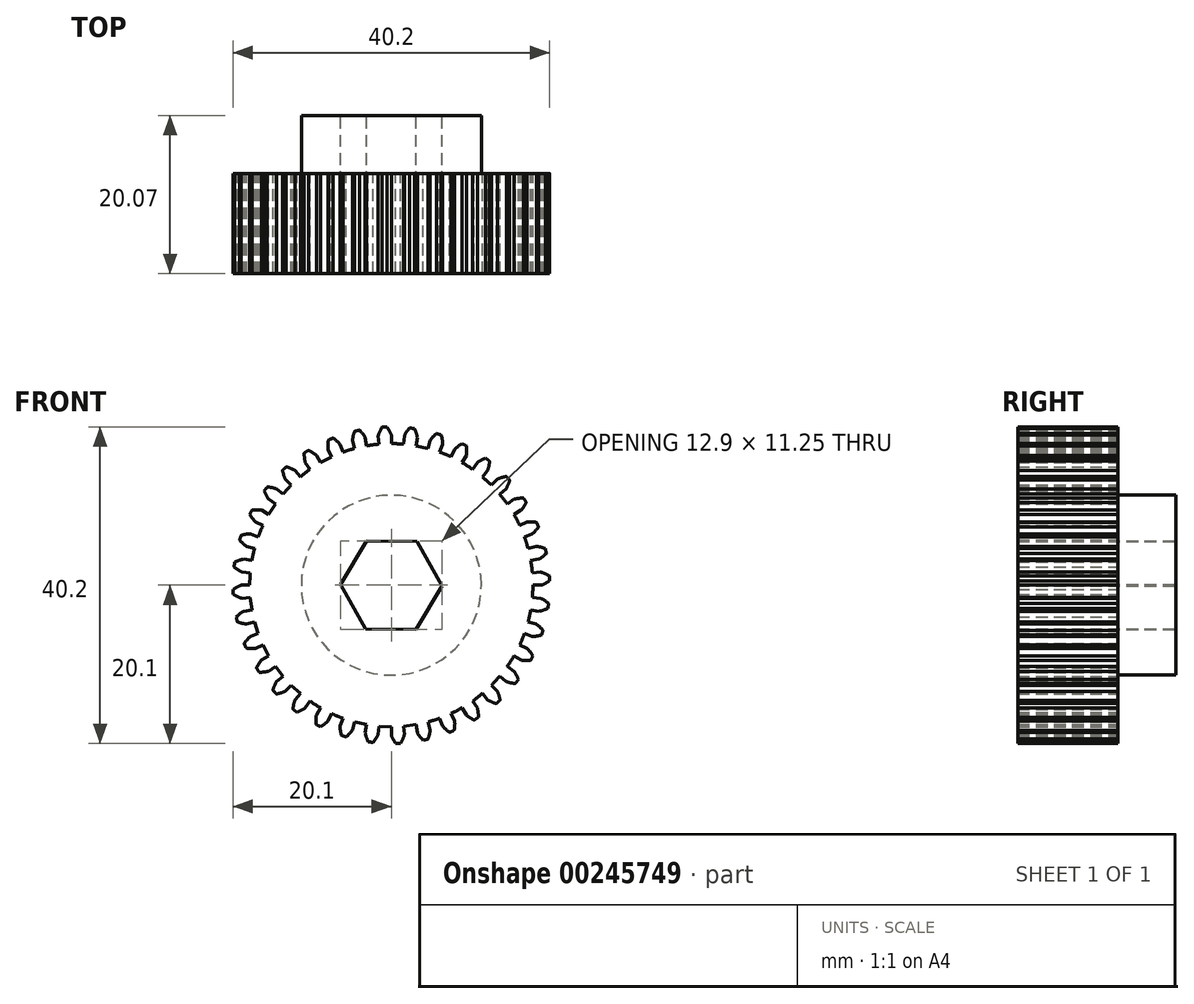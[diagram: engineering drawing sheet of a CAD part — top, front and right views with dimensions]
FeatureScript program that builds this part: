
annotation { "Feature Type Name" : "Feature", "Feature Type Description" : "" }
export const myFeature = defineFeature(function(context is Context, id is Id, definition is map)
    precondition{}
    {
        {
            var Q0;
            Q0=qCreatedBy(makeId("Front.planeOp"),FACE);
            var sketch = newSketch(context, id + "F0", { "sketchPlane" : qUnion([Q0])});
            skArc(sketch, "E0", {"start": v(-1.57, 17.91) * mm, "mid": v(-2.35, 17.83) * mm, "end": v(-3.12, 17.7) * mm});
            skLineSegment(sketch, "E1", {"start": v(0, 0) * mm, "end": v(0, 34.59) * mm});
            skLineSegment(sketch, "E2", {"start": v(0, 0) * mm, "end": v(-1.61, 36.93) * mm, "construction": true});
            skArc(sketch, "E3.trimOffspring", {"start": v(0, 19.05) * mm, "mid": v(-0.25, 19.6) * mm, "end": v(-0.56, 20.1) * mm});
            skArc(sketch, "E4.trimOffspring", {"start": v(-4.48, 17.42) * mm, "mid": v(-4.47, 17.42) * mm, "end": v(-4.47, 17.42) * mm});
            skArc(sketch, "E5.trimOffspring", {"start": v(-0.56, 20.1) * mm, "mid": v(-0.72, 20.1) * mm, "end": v(-0.88, 20.08) * mm});
            skLineSegment(sketch, "E6", {"start": v(0, 19.05) * mm, "end": v(0, 17.98) * mm});
            skArc(sketch, "E7.MirrorCS", {"start": v(-1.2, 20.07) * mm, "mid": v(-1.03, 20.08) * mm, "end": v(-0.88, 20.08) * mm});
            skArc(sketch, "E8.MirrorCS", {"start": v(-1.66, 18.98) * mm, "mid": v(-1.46, 19.54) * mm, "end": v(-1.2, 20.07) * mm});
            skLineSegment(sketch, "E9.MirrorCS", {"start": v(-1.66, 18.98) * mm, "end": v(-1.57, 17.91) * mm});
            skArc(sketch, "E10.1.0", {"start": v(-3.3, 18.76) * mm, "mid": v(-3.65, 19.25) * mm, "end": v(-4.04, 19.7) * mm});
            skArc(sketch, "E10.1.1", {"start": v(-4.93, 18.4) * mm, "mid": v(-4.83, 18.99) * mm, "end": v(-4.66, 19.56) * mm});
            skArc(sketch, "E10.1.2", {"start": v(-4.04, 19.7) * mm, "mid": v(-4.2, 19.66) * mm, "end": v(-4.35, 19.63) * mm});
            skArc(sketch, "E10.1.3", {"start": v(-4.66, 19.56) * mm, "mid": v(-4.5, 19.6) * mm, "end": v(-4.35, 19.63) * mm});
            skLineSegment(sketch, "E10.1.6", {"start": v(-4.93, 18.4) * mm, "end": v(-4.65, 17.37) * mm});
            skLineSegment(sketch, "E10.1.7", {"start": v(-3.3, 18.76) * mm, "end": v(-3.12, 17.7) * mm});
            skArc(sketch, "E10.2.0", {"start": v(-6.52, 17.9) * mm, "mid": v(-6.93, 18.32) * mm, "end": v(-7.4, 18.7) * mm});
            skArc(sketch, "E10.2.1", {"start": v(-8.05, 17.27) * mm, "mid": v(-8.05, 17.86) * mm, "end": v(-7.98, 18.45) * mm});
            skArc(sketch, "E10.2.2", {"start": v(-7.4, 18.7) * mm, "mid": v(-7.55, 18.63) * mm, "end": v(-7.7, 18.57) * mm});
            skArc(sketch, "E10.2.3", {"start": v(-7.98, 18.45) * mm, "mid": v(-7.84, 18.51) * mm, "end": v(-7.7, 18.57) * mm});
            skLineSegment(sketch, "E10.2.6", {"start": v(-8.05, 17.27) * mm, "end": v(-7.6, 16.3) * mm});
            skLineSegment(sketch, "E10.2.7", {"start": v(-6.52, 17.9) * mm, "end": v(-6.15, 16.9) * mm});
            skArc(sketch, "E10.3.0", {"start": v(-9.52, 16.5) * mm, "mid": v(-10, 16.84) * mm, "end": v(-10.53, 17.12) * mm});
            skArc(sketch, "E10.3.1", {"start": v(-10.93, 15.6) * mm, "mid": v(-11.03, 16.19) * mm, "end": v(-11.07, 16.78) * mm});
            skArc(sketch, "E10.3.2", {"start": v(-10.53, 17.12) * mm, "mid": v(-10.67, 17.04) * mm, "end": v(-10.8, 16.96) * mm});
            skArc(sketch, "E10.3.3", {"start": v(-11.07, 16.78) * mm, "mid": v(-10.93, 16.87) * mm, "end": v(-10.8, 16.96) * mm});
            skLineSegment(sketch, "E10.3.6", {"start": v(-10.93, 15.6) * mm, "end": v(-10.31, 14.73) * mm});
            skLineSegment(sketch, "E10.3.7", {"start": v(-9.52, 16.5) * mm, "end": v(-9, 15.57) * mm});
            skArc(sketch, "E10.4.0", {"start": v(-12.25, 14.6) * mm, "mid": v(-12.78, 14.85) * mm, "end": v(-13.35, 15.03) * mm});
            skArc(sketch, "E10.4.1", {"start": v(-13.47, 13.47) * mm, "mid": v(-13.68, 14.03) * mm, "end": v(-13.81, 14.6) * mm});
            skArc(sketch, "E10.4.2", {"start": v(-13.35, 15.03) * mm, "mid": v(-13.47, 14.93) * mm, "end": v(-13.58, 14.82) * mm});
            skArc(sketch, "E10.4.3", {"start": v(-13.81, 14.6) * mm, "mid": v(-13.7, 14.72) * mm, "end": v(-13.58, 14.82) * mm});
            skLineSegment(sketch, "E10.4.6", {"start": v(-13.47, 13.47) * mm, "end": v(-12.72, 12.72) * mm});
            skLineSegment(sketch, "E10.4.7", {"start": v(-12.25, 14.6) * mm, "end": v(-11.56, 13.78) * mm});
            skArc(sketch, "E10.5.0", {"start": v(-14.6, 12.25) * mm, "mid": v(-15.17, 12.4) * mm, "end": v(-15.76, 12.49) * mm});
            skArc(sketch, "E10.5.1", {"start": v(-15.6, 10.93) * mm, "mid": v(-15.9, 11.44) * mm, "end": v(-16.14, 11.99) * mm});
            skArc(sketch, "E10.5.2", {"start": v(-15.76, 12.49) * mm, "mid": v(-15.85, 12.36) * mm, "end": v(-15.95, 12.24) * mm});
            skArc(sketch, "E10.5.3", {"start": v(-16.14, 11.99) * mm, "mid": v(-16.05, 12.11) * mm, "end": v(-15.95, 12.24) * mm});
            skLineSegment(sketch, "E10.5.6", {"start": v(-15.6, 10.93) * mm, "end": v(-14.73, 10.31) * mm});
            skLineSegment(sketch, "E10.5.7", {"start": v(-14.6, 12.25) * mm, "end": v(-13.78, 11.56) * mm});
            skArc(sketch, "E10.6.0", {"start": v(-16.5, 9.53) * mm, "mid": v(-17.09, 9.58) * mm, "end": v(-17.68, 9.56) * mm});
            skArc(sketch, "E10.6.1", {"start": v(-17.27, 8.05) * mm, "mid": v(-17.65, 8.5) * mm, "end": v(-17.98, 9) * mm});
            skArc(sketch, "E10.6.2", {"start": v(-17.68, 9.56) * mm, "mid": v(-17.76, 9.42) * mm, "end": v(-17.83, 9.28) * mm});
            skArc(sketch, "E10.6.3", {"start": v(-17.98, 9) * mm, "mid": v(-17.9, 9.14) * mm, "end": v(-17.83, 9.28) * mm});
            skLineSegment(sketch, "E10.6.6", {"start": v(-17.27, 8.05) * mm, "end": v(-16.3, 7.6) * mm});
            skLineSegment(sketch, "E10.6.7", {"start": v(-16.5, 9.53) * mm, "end": v(-15.57, 9) * mm});
            skArc(sketch, "E10.7.0", {"start": v(-17.9, 6.52) * mm, "mid": v(-18.5, 6.47) * mm, "end": v(-19.08, 6.35) * mm});
            skArc(sketch, "E10.7.1", {"start": v(-18.4, 4.93) * mm, "mid": v(-18.86, 5.3) * mm, "end": v(-19.27, 5.74) * mm});
            skArc(sketch, "E10.7.2", {"start": v(-19.08, 6.35) * mm, "mid": v(-19.13, 6.2) * mm, "end": v(-19.17, 6.05) * mm});
            skArc(sketch, "E10.7.3", {"start": v(-19.27, 5.74) * mm, "mid": v(-19.22, 5.9) * mm, "end": v(-19.17, 6.05) * mm});
            skLineSegment(sketch, "E10.7.6", {"start": v(-18.4, 4.93) * mm, "end": v(-17.37, 4.65) * mm});
            skLineSegment(sketch, "E10.7.7", {"start": v(-17.9, 6.52) * mm, "end": v(-16.9, 6.15) * mm});
            skArc(sketch, "E10.8.0", {"start": v(-18.76, 3.3) * mm, "mid": v(-19.34, 3.16) * mm, "end": v(-19.89, 2.94) * mm});
            skArc(sketch, "E10.8.1", {"start": v(-18.98, 1.66) * mm, "mid": v(-19.5, 1.95) * mm, "end": v(-19.97, 2.31) * mm});
            skArc(sketch, "E10.8.2", {"start": v(-19.89, 2.94) * mm, "mid": v(-19.91, 2.78) * mm, "end": v(-19.93, 2.62) * mm});
            skArc(sketch, "E10.8.3", {"start": v(-19.97, 2.31) * mm, "mid": v(-19.95, 2.47) * mm, "end": v(-19.93, 2.62) * mm});
            skLineSegment(sketch, "E10.8.6", {"start": v(-18.98, 1.66) * mm, "end": v(-17.91, 1.57) * mm});
            skLineSegment(sketch, "E10.8.7", {"start": v(-18.76, 3.3) * mm, "end": v(-17.7, 3.12) * mm});
            skArc(sketch, "E10.9.0", {"start": v(-19.05, 0) * mm, "mid": v(-19.6, -0.25) * mm, "end": v(-20.1, -0.56) * mm});
            skArc(sketch, "E10.9.1", {"start": v(-18.98, -1.66) * mm, "mid": v(-19.54, -1.46) * mm, "end": v(-20.07, -1.2) * mm});
            skArc(sketch, "E10.9.2", {"start": v(-20.1, -0.56) * mm, "mid": v(-20.1, -0.72) * mm, "end": v(-20.08, -0.88) * mm});
            skArc(sketch, "E10.9.3", {"start": v(-20.07, -1.2) * mm, "mid": v(-20.08, -1.03) * mm, "end": v(-20.08, -0.88) * mm});
            skLineSegment(sketch, "E10.9.6", {"start": v(-18.98, -1.66) * mm, "end": v(-17.91, -1.57) * mm});
            skLineSegment(sketch, "E10.9.7", {"start": v(-19.05, 0) * mm, "end": v(-17.98, 0) * mm});
            skArc(sketch, "E10.10.0", {"start": v(-18.76, -3.3) * mm, "mid": v(-19.25, -3.65) * mm, "end": v(-19.7, -4.04) * mm});
            skArc(sketch, "E10.10.1", {"start": v(-18.4, -4.93) * mm, "mid": v(-18.99, -4.83) * mm, "end": v(-19.56, -4.66) * mm});
            skArc(sketch, "E10.10.2", {"start": v(-19.7, -4.04) * mm, "mid": v(-19.66, -4.2) * mm, "end": v(-19.63, -4.35) * mm});
            skArc(sketch, "E10.10.3", {"start": v(-19.56, -4.66) * mm, "mid": v(-19.6, -4.5) * mm, "end": v(-19.63, -4.35) * mm});
            skLineSegment(sketch, "E10.10.6", {"start": v(-18.4, -4.93) * mm, "end": v(-17.37, -4.65) * mm});
            skLineSegment(sketch, "E10.10.7", {"start": v(-18.76, -3.3) * mm, "end": v(-17.7, -3.12) * mm});
            skArc(sketch, "E10.11.0", {"start": v(-17.9, -6.52) * mm, "mid": v(-18.32, -6.93) * mm, "end": v(-18.7, -7.4) * mm});
            skArc(sketch, "E10.11.1", {"start": v(-17.27, -8.05) * mm, "mid": v(-17.86, -8.05) * mm, "end": v(-18.45, -7.98) * mm});
            skArc(sketch, "E10.11.2", {"start": v(-18.7, -7.4) * mm, "mid": v(-18.63, -7.55) * mm, "end": v(-18.57, -7.7) * mm});
            skArc(sketch, "E10.11.3", {"start": v(-18.45, -7.98) * mm, "mid": v(-18.51, -7.84) * mm, "end": v(-18.57, -7.7) * mm});
            skLineSegment(sketch, "E10.11.6", {"start": v(-17.27, -8.05) * mm, "end": v(-16.3, -7.6) * mm});
            skLineSegment(sketch, "E10.11.7", {"start": v(-17.9, -6.52) * mm, "end": v(-16.9, -6.15) * mm});
            skArc(sketch, "E10.12.0", {"start": v(-16.5, -9.52) * mm, "mid": v(-16.84, -10) * mm, "end": v(-17.12, -10.53) * mm});
            skArc(sketch, "E10.12.1", {"start": v(-15.6, -10.93) * mm, "mid": v(-16.19, -11.03) * mm, "end": v(-16.78, -11.07) * mm});
            skArc(sketch, "E10.12.2", {"start": v(-17.12, -10.53) * mm, "mid": v(-17.04, -10.67) * mm, "end": v(-16.96, -10.8) * mm});
            skArc(sketch, "E10.12.3", {"start": v(-16.78, -11.07) * mm, "mid": v(-16.87, -10.93) * mm, "end": v(-16.96, -10.8) * mm});
            skLineSegment(sketch, "E10.12.6", {"start": v(-15.6, -10.93) * mm, "end": v(-14.73, -10.31) * mm});
            skLineSegment(sketch, "E10.12.7", {"start": v(-16.5, -9.52) * mm, "end": v(-15.57, -9) * mm});
            skArc(sketch, "E10.13.0", {"start": v(-14.6, -12.25) * mm, "mid": v(-14.85, -12.78) * mm, "end": v(-15.03, -13.35) * mm});
            skArc(sketch, "E10.13.1", {"start": v(-13.47, -13.47) * mm, "mid": v(-14.03, -13.68) * mm, "end": v(-14.6, -13.81) * mm});
            skArc(sketch, "E10.13.2", {"start": v(-15.03, -13.35) * mm, "mid": v(-14.93, -13.47) * mm, "end": v(-14.82, -13.58) * mm});
            skArc(sketch, "E10.13.3", {"start": v(-14.6, -13.81) * mm, "mid": v(-14.72, -13.7) * mm, "end": v(-14.82, -13.58) * mm});
            skLineSegment(sketch, "E10.13.6", {"start": v(-13.47, -13.47) * mm, "end": v(-12.72, -12.72) * mm});
            skLineSegment(sketch, "E10.13.7", {"start": v(-14.6, -12.25) * mm, "end": v(-13.78, -11.56) * mm});
            skArc(sketch, "E10.14.0", {"start": v(-12.25, -14.6) * mm, "mid": v(-12.4, -15.17) * mm, "end": v(-12.49, -15.76) * mm});
            skArc(sketch, "E10.14.1", {"start": v(-10.93, -15.6) * mm, "mid": v(-11.44, -15.9) * mm, "end": v(-11.99, -16.14) * mm});
            skArc(sketch, "E10.14.2", {"start": v(-12.49, -15.76) * mm, "mid": v(-12.36, -15.85) * mm, "end": v(-12.24, -15.95) * mm});
            skArc(sketch, "E10.14.3", {"start": v(-11.99, -16.14) * mm, "mid": v(-12.11, -16.05) * mm, "end": v(-12.24, -15.95) * mm});
            skLineSegment(sketch, "E10.14.6", {"start": v(-10.93, -15.6) * mm, "end": v(-10.31, -14.73) * mm});
            skLineSegment(sketch, "E10.14.7", {"start": v(-12.25, -14.6) * mm, "end": v(-11.56, -13.78) * mm});
            skArc(sketch, "E10.15.0", {"start": v(-9.53, -16.5) * mm, "mid": v(-9.58, -17.09) * mm, "end": v(-9.56, -17.68) * mm});
            skArc(sketch, "E10.15.1", {"start": v(-8.05, -17.27) * mm, "mid": v(-8.5, -17.65) * mm, "end": v(-9, -17.98) * mm});
            skArc(sketch, "E10.15.2", {"start": v(-9.56, -17.68) * mm, "mid": v(-9.42, -17.76) * mm, "end": v(-9.28, -17.83) * mm});
            skArc(sketch, "E10.15.3", {"start": v(-9, -17.98) * mm, "mid": v(-9.14, -17.9) * mm, "end": v(-9.28, -17.83) * mm});
            skLineSegment(sketch, "E10.15.6", {"start": v(-8.05, -17.27) * mm, "end": v(-7.6, -16.3) * mm});
            skLineSegment(sketch, "E10.15.7", {"start": v(-9.53, -16.5) * mm, "end": v(-9, -15.57) * mm});
            skArc(sketch, "E10.16.0", {"start": v(-6.52, -17.9) * mm, "mid": v(-6.47, -18.5) * mm, "end": v(-6.35, -19.08) * mm});
            skArc(sketch, "E10.16.1", {"start": v(-4.93, -18.4) * mm, "mid": v(-5.3, -18.86) * mm, "end": v(-5.74, -19.27) * mm});
            skArc(sketch, "E10.16.2", {"start": v(-6.35, -19.08) * mm, "mid": v(-6.2, -19.13) * mm, "end": v(-6.05, -19.17) * mm});
            skArc(sketch, "E10.16.3", {"start": v(-5.74, -19.27) * mm, "mid": v(-5.9, -19.22) * mm, "end": v(-6.05, -19.17) * mm});
            skLineSegment(sketch, "E10.16.6", {"start": v(-4.93, -18.4) * mm, "end": v(-4.65, -17.37) * mm});
            skLineSegment(sketch, "E10.16.7", {"start": v(-6.52, -17.9) * mm, "end": v(-6.15, -16.9) * mm});
            skArc(sketch, "E10.17.0", {"start": v(-3.3, -18.76) * mm, "mid": v(-3.16, -19.34) * mm, "end": v(-2.94, -19.89) * mm});
            skArc(sketch, "E10.17.1", {"start": v(-1.66, -18.98) * mm, "mid": v(-1.95, -19.5) * mm, "end": v(-2.31, -19.97) * mm});
            skArc(sketch, "E10.17.2", {"start": v(-2.94, -19.89) * mm, "mid": v(-2.78, -19.91) * mm, "end": v(-2.62, -19.93) * mm});
            skArc(sketch, "E10.17.3", {"start": v(-2.31, -19.97) * mm, "mid": v(-2.47, -19.95) * mm, "end": v(-2.62, -19.93) * mm});
            skLineSegment(sketch, "E10.17.6", {"start": v(-1.66, -18.98) * mm, "end": v(-1.57, -17.91) * mm});
            skLineSegment(sketch, "E10.17.7", {"start": v(-3.3, -18.76) * mm, "end": v(-3.12, -17.7) * mm});
            skArc(sketch, "E10.18.0", {"start": v(0, -19.05) * mm, "mid": v(0.25, -19.6) * mm, "end": v(0.56, -20.1) * mm});
            skArc(sketch, "E10.18.1", {"start": v(1.66, -18.98) * mm, "mid": v(1.46, -19.54) * mm, "end": v(1.2, -20.07) * mm});
            skArc(sketch, "E10.18.2", {"start": v(0.56, -20.1) * mm, "mid": v(0.72, -20.1) * mm, "end": v(0.88, -20.08) * mm});
            skArc(sketch, "E10.18.3", {"start": v(1.2, -20.07) * mm, "mid": v(1.03, -20.08) * mm, "end": v(0.88, -20.08) * mm});
            skLineSegment(sketch, "E10.18.6", {"start": v(1.66, -18.98) * mm, "end": v(1.57, -17.91) * mm});
            skLineSegment(sketch, "E10.18.7", {"start": v(0, -19.05) * mm, "end": v(0, -17.98) * mm});
            skArc(sketch, "E10.19.0", {"start": v(3.3, -18.76) * mm, "mid": v(3.65, -19.25) * mm, "end": v(4.04, -19.7) * mm});
            skArc(sketch, "E10.19.1", {"start": v(4.93, -18.4) * mm, "mid": v(4.83, -18.99) * mm, "end": v(4.66, -19.56) * mm});
            skArc(sketch, "E10.19.2", {"start": v(4.04, -19.7) * mm, "mid": v(4.2, -19.66) * mm, "end": v(4.35, -19.63) * mm});
            skArc(sketch, "E10.19.3", {"start": v(4.66, -19.56) * mm, "mid": v(4.5, -19.6) * mm, "end": v(4.35, -19.63) * mm});
            skLineSegment(sketch, "E10.19.6", {"start": v(4.93, -18.4) * mm, "end": v(4.65, -17.37) * mm});
            skLineSegment(sketch, "E10.19.7", {"start": v(3.3, -18.76) * mm, "end": v(3.12, -17.7) * mm});
            skArc(sketch, "E10.20.0", {"start": v(6.52, -17.9) * mm, "mid": v(6.93, -18.32) * mm, "end": v(7.4, -18.7) * mm});
            skArc(sketch, "E10.20.1", {"start": v(8.05, -17.27) * mm, "mid": v(8.05, -17.86) * mm, "end": v(7.98, -18.45) * mm});
            skArc(sketch, "E10.20.2", {"start": v(7.4, -18.7) * mm, "mid": v(7.55, -18.63) * mm, "end": v(7.7, -18.57) * mm});
            skArc(sketch, "E10.20.3", {"start": v(7.98, -18.45) * mm, "mid": v(7.84, -18.51) * mm, "end": v(7.7, -18.57) * mm});
            skLineSegment(sketch, "E10.20.6", {"start": v(8.05, -17.27) * mm, "end": v(7.6, -16.3) * mm});
            skLineSegment(sketch, "E10.20.7", {"start": v(6.52, -17.9) * mm, "end": v(6.15, -16.9) * mm});
            skArc(sketch, "E10.21.0", {"start": v(9.52, -16.5) * mm, "mid": v(10, -16.84) * mm, "end": v(10.53, -17.12) * mm});
            skArc(sketch, "E10.21.1", {"start": v(10.93, -15.6) * mm, "mid": v(11.03, -16.19) * mm, "end": v(11.07, -16.78) * mm});
            skArc(sketch, "E10.21.2", {"start": v(10.53, -17.12) * mm, "mid": v(10.67, -17.04) * mm, "end": v(10.8, -16.96) * mm});
            skArc(sketch, "E10.21.3", {"start": v(11.07, -16.78) * mm, "mid": v(10.93, -16.87) * mm, "end": v(10.8, -16.96) * mm});
            skLineSegment(sketch, "E10.21.6", {"start": v(10.93, -15.6) * mm, "end": v(10.31, -14.73) * mm});
            skLineSegment(sketch, "E10.21.7", {"start": v(9.53, -16.5) * mm, "end": v(9, -15.57) * mm});
            skArc(sketch, "E10.22.0", {"start": v(12.25, -14.6) * mm, "mid": v(12.78, -14.85) * mm, "end": v(13.35, -15.03) * mm});
            skArc(sketch, "E10.22.1", {"start": v(13.47, -13.47) * mm, "mid": v(13.68, -14.03) * mm, "end": v(13.81, -14.6) * mm});
            skArc(sketch, "E10.22.2", {"start": v(13.35, -15.03) * mm, "mid": v(13.47, -14.93) * mm, "end": v(13.58, -14.82) * mm});
            skArc(sketch, "E10.22.3", {"start": v(13.81, -14.6) * mm, "mid": v(13.7, -14.72) * mm, "end": v(13.58, -14.82) * mm});
            skLineSegment(sketch, "E10.22.6", {"start": v(13.47, -13.47) * mm, "end": v(12.72, -12.72) * mm});
            skLineSegment(sketch, "E10.22.7", {"start": v(12.25, -14.6) * mm, "end": v(11.56, -13.78) * mm});
            skArc(sketch, "E10.23.0", {"start": v(14.6, -12.25) * mm, "mid": v(15.17, -12.4) * mm, "end": v(15.76, -12.49) * mm});
            skArc(sketch, "E10.23.1", {"start": v(15.6, -10.93) * mm, "mid": v(15.9, -11.44) * mm, "end": v(16.14, -11.99) * mm});
            skArc(sketch, "E10.23.2", {"start": v(15.76, -12.49) * mm, "mid": v(15.85, -12.36) * mm, "end": v(15.95, -12.24) * mm});
            skArc(sketch, "E10.23.3", {"start": v(16.14, -11.99) * mm, "mid": v(16.05, -12.11) * mm, "end": v(15.95, -12.24) * mm});
            skLineSegment(sketch, "E10.23.6", {"start": v(15.6, -10.93) * mm, "end": v(14.73, -10.31) * mm});
            skLineSegment(sketch, "E10.23.7", {"start": v(14.6, -12.25) * mm, "end": v(13.78, -11.56) * mm});
            skArc(sketch, "E10.24.0", {"start": v(16.5, -9.53) * mm, "mid": v(17.09, -9.58) * mm, "end": v(17.68, -9.56) * mm});
            skArc(sketch, "E10.24.1", {"start": v(17.27, -8.05) * mm, "mid": v(17.65, -8.5) * mm, "end": v(17.98, -9) * mm});
            skArc(sketch, "E10.24.2", {"start": v(17.68, -9.56) * mm, "mid": v(17.76, -9.42) * mm, "end": v(17.83, -9.28) * mm});
            skArc(sketch, "E10.24.3", {"start": v(17.98, -9) * mm, "mid": v(17.9, -9.14) * mm, "end": v(17.83, -9.28) * mm});
            skLineSegment(sketch, "E10.24.6", {"start": v(17.27, -8.05) * mm, "end": v(16.3, -7.6) * mm});
            skLineSegment(sketch, "E10.24.7", {"start": v(16.5, -9.53) * mm, "end": v(15.57, -9) * mm});
            skArc(sketch, "E10.25.0", {"start": v(17.9, -6.52) * mm, "mid": v(18.5, -6.47) * mm, "end": v(19.08, -6.35) * mm});
            skArc(sketch, "E10.25.1", {"start": v(18.4, -4.93) * mm, "mid": v(18.86, -5.3) * mm, "end": v(19.27, -5.74) * mm});
            skArc(sketch, "E10.25.2", {"start": v(19.08, -6.35) * mm, "mid": v(19.13, -6.2) * mm, "end": v(19.17, -6.05) * mm});
            skArc(sketch, "E10.25.3", {"start": v(19.27, -5.74) * mm, "mid": v(19.22, -5.9) * mm, "end": v(19.17, -6.05) * mm});
            skLineSegment(sketch, "E10.25.6", {"start": v(18.4, -4.93) * mm, "end": v(17.37, -4.65) * mm});
            skLineSegment(sketch, "E10.25.7", {"start": v(17.9, -6.52) * mm, "end": v(16.9, -6.15) * mm});
            skArc(sketch, "E10.26.0", {"start": v(18.76, -3.3) * mm, "mid": v(19.34, -3.16) * mm, "end": v(19.89, -2.94) * mm});
            skArc(sketch, "E10.26.1", {"start": v(18.98, -1.66) * mm, "mid": v(19.5, -1.95) * mm, "end": v(19.97, -2.31) * mm});
            skArc(sketch, "E10.26.2", {"start": v(19.89, -2.94) * mm, "mid": v(19.91, -2.78) * mm, "end": v(19.93, -2.62) * mm});
            skArc(sketch, "E10.26.3", {"start": v(19.97, -2.31) * mm, "mid": v(19.95, -2.47) * mm, "end": v(19.93, -2.62) * mm});
            skLineSegment(sketch, "E10.26.6", {"start": v(18.98, -1.66) * mm, "end": v(17.91, -1.57) * mm});
            skLineSegment(sketch, "E10.26.7", {"start": v(18.76, -3.3) * mm, "end": v(17.7, -3.12) * mm});
            skArc(sketch, "E10.27.0", {"start": v(19.05, 0) * mm, "mid": v(19.6, 0.25) * mm, "end": v(20.1, 0.56) * mm});
            skArc(sketch, "E10.27.1", {"start": v(18.98, 1.66) * mm, "mid": v(19.54, 1.46) * mm, "end": v(20.07, 1.2) * mm});
            skArc(sketch, "E10.27.2", {"start": v(20.1, 0.56) * mm, "mid": v(20.1, 0.72) * mm, "end": v(20.08, 0.88) * mm});
            skArc(sketch, "E10.27.3", {"start": v(20.07, 1.2) * mm, "mid": v(20.08, 1.03) * mm, "end": v(20.08, 0.88) * mm});
            skLineSegment(sketch, "E10.27.6", {"start": v(18.98, 1.66) * mm, "end": v(17.91, 1.57) * mm});
            skLineSegment(sketch, "E10.27.7", {"start": v(19.05, 0) * mm, "end": v(17.98, 0) * mm});
            skArc(sketch, "E10.28.0", {"start": v(18.76, 3.3) * mm, "mid": v(19.25, 3.65) * mm, "end": v(19.7, 4.04) * mm});
            skArc(sketch, "E10.28.1", {"start": v(18.4, 4.93) * mm, "mid": v(18.99, 4.83) * mm, "end": v(19.56, 4.66) * mm});
            skArc(sketch, "E10.28.2", {"start": v(19.7, 4.04) * mm, "mid": v(19.66, 4.2) * mm, "end": v(19.63, 4.35) * mm});
            skArc(sketch, "E10.28.3", {"start": v(19.56, 4.66) * mm, "mid": v(19.6, 4.5) * mm, "end": v(19.63, 4.35) * mm});
            skLineSegment(sketch, "E10.28.6", {"start": v(18.4, 4.93) * mm, "end": v(17.37, 4.65) * mm});
            skLineSegment(sketch, "E10.28.7", {"start": v(18.76, 3.3) * mm, "end": v(17.7, 3.12) * mm});
            skArc(sketch, "E10.29.0", {"start": v(17.9, 6.52) * mm, "mid": v(18.32, 6.93) * mm, "end": v(18.7, 7.4) * mm});
            skArc(sketch, "E10.29.1", {"start": v(17.27, 8.05) * mm, "mid": v(17.86, 8.05) * mm, "end": v(18.45, 7.98) * mm});
            skArc(sketch, "E10.29.2", {"start": v(18.7, 7.4) * mm, "mid": v(18.63, 7.55) * mm, "end": v(18.57, 7.7) * mm});
            skArc(sketch, "E10.29.3", {"start": v(18.45, 7.98) * mm, "mid": v(18.51, 7.84) * mm, "end": v(18.57, 7.7) * mm});
            skLineSegment(sketch, "E10.29.6", {"start": v(17.27, 8.05) * mm, "end": v(16.3, 7.6) * mm});
            skLineSegment(sketch, "E10.29.7", {"start": v(17.9, 6.52) * mm, "end": v(16.9, 6.15) * mm});
            skArc(sketch, "E10.30.0", {"start": v(16.5, 9.52) * mm, "mid": v(16.84, 10) * mm, "end": v(17.12, 10.53) * mm});
            skArc(sketch, "E10.30.1", {"start": v(15.6, 10.93) * mm, "mid": v(16.19, 11.03) * mm, "end": v(16.78, 11.07) * mm});
            skArc(sketch, "E10.30.2", {"start": v(17.12, 10.53) * mm, "mid": v(17.04, 10.67) * mm, "end": v(16.96, 10.8) * mm});
            skArc(sketch, "E10.30.3", {"start": v(16.78, 11.07) * mm, "mid": v(16.87, 10.93) * mm, "end": v(16.96, 10.8) * mm});
            skLineSegment(sketch, "E10.30.6", {"start": v(15.6, 10.93) * mm, "end": v(14.73, 10.31) * mm});
            skLineSegment(sketch, "E10.30.7", {"start": v(16.5, 9.52) * mm, "end": v(15.57, 9) * mm});
            skArc(sketch, "E10.31.0", {"start": v(14.6, 12.25) * mm, "mid": v(14.85, 12.78) * mm, "end": v(15.03, 13.35) * mm});
            skArc(sketch, "E10.31.1", {"start": v(13.47, 13.47) * mm, "mid": v(14.03, 13.68) * mm, "end": v(14.6, 13.81) * mm});
            skArc(sketch, "E10.31.2", {"start": v(15.03, 13.35) * mm, "mid": v(14.93, 13.47) * mm, "end": v(14.82, 13.58) * mm});
            skArc(sketch, "E10.31.3", {"start": v(14.6, 13.81) * mm, "mid": v(14.72, 13.7) * mm, "end": v(14.82, 13.58) * mm});
            skLineSegment(sketch, "E10.31.6", {"start": v(13.47, 13.47) * mm, "end": v(12.72, 12.72) * mm});
            skLineSegment(sketch, "E10.31.7", {"start": v(14.6, 12.25) * mm, "end": v(13.78, 11.56) * mm});
            skArc(sketch, "E10.32.0", {"start": v(12.25, 14.6) * mm, "mid": v(12.4, 15.17) * mm, "end": v(12.49, 15.76) * mm});
            skArc(sketch, "E10.32.1", {"start": v(10.93, 15.6) * mm, "mid": v(11.44, 15.9) * mm, "end": v(11.99, 16.14) * mm});
            skArc(sketch, "E10.32.2", {"start": v(12.49, 15.76) * mm, "mid": v(12.36, 15.85) * mm, "end": v(12.24, 15.95) * mm});
            skArc(sketch, "E10.32.3", {"start": v(11.99, 16.14) * mm, "mid": v(12.11, 16.05) * mm, "end": v(12.24, 15.95) * mm});
            skLineSegment(sketch, "E10.32.6", {"start": v(10.93, 15.6) * mm, "end": v(10.31, 14.73) * mm});
            skLineSegment(sketch, "E10.32.7", {"start": v(12.25, 14.6) * mm, "end": v(11.56, 13.78) * mm});
            skArc(sketch, "E10.33.0", {"start": v(9.53, 16.5) * mm, "mid": v(9.58, 17.09) * mm, "end": v(9.56, 17.68) * mm});
            skArc(sketch, "E10.33.1", {"start": v(8.05, 17.27) * mm, "mid": v(8.5, 17.65) * mm, "end": v(9, 17.98) * mm});
            skArc(sketch, "E10.33.2", {"start": v(9.56, 17.68) * mm, "mid": v(9.42, 17.76) * mm, "end": v(9.28, 17.83) * mm});
            skArc(sketch, "E10.33.3", {"start": v(9, 17.98) * mm, "mid": v(9.14, 17.9) * mm, "end": v(9.28, 17.83) * mm});
            skLineSegment(sketch, "E10.33.6", {"start": v(8.05, 17.27) * mm, "end": v(7.6, 16.3) * mm});
            skLineSegment(sketch, "E10.33.7", {"start": v(9.52, 16.5) * mm, "end": v(9, 15.57) * mm});
            skArc(sketch, "E10.34.0", {"start": v(6.52, 17.9) * mm, "mid": v(6.47, 18.5) * mm, "end": v(6.35, 19.08) * mm});
            skArc(sketch, "E10.34.1", {"start": v(4.93, 18.4) * mm, "mid": v(5.3, 18.86) * mm, "end": v(5.74, 19.27) * mm});
            skArc(sketch, "E10.34.2", {"start": v(6.35, 19.08) * mm, "mid": v(6.2, 19.13) * mm, "end": v(6.05, 19.17) * mm});
            skArc(sketch, "E10.34.3", {"start": v(5.74, 19.27) * mm, "mid": v(5.9, 19.22) * mm, "end": v(6.05, 19.17) * mm});
            skLineSegment(sketch, "E10.34.6", {"start": v(4.93, 18.4) * mm, "end": v(4.65, 17.37) * mm});
            skLineSegment(sketch, "E10.34.7", {"start": v(6.52, 17.9) * mm, "end": v(6.15, 16.9) * mm});
            skArc(sketch, "E10.35.0", {"start": v(3.3, 18.76) * mm, "mid": v(3.16, 19.34) * mm, "end": v(2.94, 19.89) * mm});
            skArc(sketch, "E10.35.1", {"start": v(1.66, 18.98) * mm, "mid": v(1.95, 19.5) * mm, "end": v(2.31, 19.97) * mm});
            skArc(sketch, "E10.35.2", {"start": v(2.94, 19.89) * mm, "mid": v(2.78, 19.91) * mm, "end": v(2.62, 19.93) * mm});
            skArc(sketch, "E10.35.3", {"start": v(2.31, 19.97) * mm, "mid": v(2.47, 19.95) * mm, "end": v(2.62, 19.93) * mm});
            skLineSegment(sketch, "E10.35.6", {"start": v(1.66, 18.98) * mm, "end": v(1.57, 17.91) * mm});
            skLineSegment(sketch, "E10.35.7", {"start": v(3.3, 18.76) * mm, "end": v(3.12, 17.7) * mm});
            skArc(sketch, "E11.trimOffspring", {"start": v(-4.65, 17.37) * mm, "mid": v(-5.4, 17.15) * mm, "end": v(-6.15, 16.9) * mm});
            skArc(sketch, "E12.trimOffspring", {"start": v(1.57, 17.91) * mm, "mid": v(0.78, 17.97) * mm, "end": v(0, 17.98) * mm});
            skArc(sketch, "E13.trimOffspring", {"start": v(7.6, 16.3) * mm, "mid": v(6.88, 16.61) * mm, "end": v(6.15, 16.9) * mm});
            skArc(sketch, "E14.trimOffspring", {"start": v(10.31, 14.73) * mm, "mid": v(9.66, 15.17) * mm, "end": v(9, 15.57) * mm});
            skArc(sketch, "E15.trimOffspring", {"start": v(12.72, 12.72) * mm, "mid": v(12.15, 13.26) * mm, "end": v(11.56, 13.78) * mm});
            skArc(sketch, "E16.trimOffspring", {"start": v(14.73, 10.31) * mm, "mid": v(14.27, 10.95) * mm, "end": v(13.78, 11.56) * mm});
            skArc(sketch, "E17.trimOffspring", {"start": v(16.3, 7.6) * mm, "mid": v(15.95, 8.3) * mm, "end": v(15.57, 9) * mm});
            skArc(sketch, "E18.trimOffspring", {"start": v(17.37, 4.65) * mm, "mid": v(17.15, 5.4) * mm, "end": v(16.9, 6.15) * mm});
            skArc(sketch, "E19.trimOffspring", {"start": v(17.91, 1.57) * mm, "mid": v(17.83, 2.35) * mm, "end": v(17.7, 3.12) * mm});
            skArc(sketch, "E20.trimOffspring", {"start": v(17.91, -1.57) * mm, "mid": v(17.97, -0.78) * mm, "end": v(17.98, 0) * mm});
            skArc(sketch, "E21.trimOffspring", {"start": v(17.37, -4.65) * mm, "mid": v(17.56, -3.9) * mm, "end": v(17.7, -3.12) * mm});
            skArc(sketch, "E22.trimOffspring", {"start": v(16.3, -7.6) * mm, "mid": v(16.61, -6.88) * mm, "end": v(16.9, -6.15) * mm});
            skArc(sketch, "E23.trimOffspring", {"start": v(14.73, -10.31) * mm, "mid": v(15.17, -9.66) * mm, "end": v(15.57, -9) * mm});
            skArc(sketch, "E24.trimOffspring", {"start": v(12.72, -12.72) * mm, "mid": v(13.26, -12.15) * mm, "end": v(13.78, -11.56) * mm});
            skArc(sketch, "E25.trimOffspring", {"start": v(10.31, -14.73) * mm, "mid": v(10.95, -14.27) * mm, "end": v(11.56, -13.78) * mm});
            skArc(sketch, "E26.trimOffspring", {"start": v(7.6, -16.3) * mm, "mid": v(8.3, -15.95) * mm, "end": v(9, -15.57) * mm});
            skArc(sketch, "E27.trimOffspring", {"start": v(4.65, -17.37) * mm, "mid": v(5.4, -17.15) * mm, "end": v(6.15, -16.9) * mm});
            skArc(sketch, "E28.trimOffspring", {"start": v(-10.31, 14.73) * mm, "mid": v(-10.95, 14.27) * mm, "end": v(-11.56, 13.78) * mm});
            skArc(sketch, "E29.trimOffspring", {"start": v(-12.72, 12.72) * mm, "mid": v(-13.26, 12.15) * mm, "end": v(-13.78, 11.56) * mm});
            skArc(sketch, "E30.trimOffspring", {"start": v(-16.3, 7.6) * mm, "mid": v(-16.61, 6.88) * mm, "end": v(-16.9, 6.15) * mm});
            skArc(sketch, "E31.trimOffspring", {"start": v(-17.37, 4.65) * mm, "mid": v(-17.56, 3.9) * mm, "end": v(-17.7, 3.12) * mm});
            skArc(sketch, "E32.trimOffspring", {"start": v(-17.91, 1.57) * mm, "mid": v(-17.97, 0.78) * mm, "end": v(-17.98, 0) * mm});
            skArc(sketch, "E33.trimOffspring", {"start": v(-10.31, -14.73) * mm, "mid": v(-9.66, -15.17) * mm, "end": v(-9, -15.57) * mm});
            skArc(sketch, "E34.trimOffspring", {"start": v(-7.6, -16.3) * mm, "mid": v(-6.88, -16.61) * mm, "end": v(-6.15, -16.9) * mm});
            skLineSegment(sketch, "E35", {"start": v(-16.3, -7.6) * mm, "end": v(-15.57, -9) * mm});
            skLineSegment(sketch, "E36", {"start": v(-17.37, -4.65) * mm, "end": v(-16.9, -6.15) * mm});
            skLineSegment(sketch, "E37", {"start": v(-14.73, -10.31) * mm, "end": v(-13.78, -11.56) * mm});
            skLineSegment(sketch, "E38", {"start": v(-12.72, -12.72) * mm, "end": v(-11.56, -13.78) * mm});
            skLineSegment(sketch, "E39", {"start": v(-4.65, -17.37) * mm, "end": v(-3.12, -17.7) * mm});
            skLineSegment(sketch, "E40", {"start": v(-1.57, -17.91) * mm, "end": v(0, -17.98) * mm});
            skLineSegment(sketch, "E41", {"start": v(1.57, -17.91) * mm, "end": v(3.12, -17.7) * mm});
            skLineSegment(sketch, "E42", {"start": v(-17.91, -1.57) * mm, "end": v(-17.7, -3.12) * mm});
            skLineSegment(sketch, "E43", {"start": v(-15.57, 9) * mm, "end": v(-14.73, 10.31) * mm});
            skLineSegment(sketch, "E44", {"start": v(-9, 15.57) * mm, "end": v(-7.6, 16.3) * mm});
            skLineSegment(sketch, "E45", {"start": v(3.12, 17.7) * mm, "end": v(4.65, 17.37) * mm});
            skSolve(sketch);
        }
        {
            var Q0;
            Q0 = qSketchRegion(id + "F0", true);
            extrude(context, id + "F1", {"entities" : qUnion([Q0]), "depth" : 12.7 * mm});
        }
        {
            var Q0;
            Q0=qCreatedBy(makeId("Front.planeOp"),FACE);
            var sketch = newSketch(context, id + "F2", { "sketchPlane" : qUnion([Q0])});
            skCircle(sketch, "E46", {"center": v(0, 0) * mm, "radius": 11.43 * mm});
            skSolve(sketch);
        }
        {
            var Q0;
            Q0=makeQuery(id+"F2.imprint","IMPRINT",FACE,{"disambiguationData":[TD([[makeQuery(id+"F2.imprint","IMPRINT",EDGE,{"derivedFrom":sQuery(id+"F2.wireOp",EDGE,"E46")}),1.0]])]});
            extrude(context, id + "F3", {"entities" : qUnion([Q0]), "operationType" : NewBodyOperationType.ADD, "oppositeDirection" : true, "depth" : 7.37 * mm});
        }
        {
            var Q0;
            Q0=makeQuery(id+"F3.opExtrude","CAP_FACE",FACE,{"disambiguationData":[OSD([sQuery(id+"F2.wireOp",EDGE,"E46")])],"isStart":false});
            var sketch = newSketch(context, id + "F4", { "sketchPlane" : qUnion([Q0])});
            skCircle(sketch, "E47.cCircle", {"center": v(0, 0) * mm, "radius": 6.45 * mm, "construction": true});
            skLineSegment(sketch, "E47.0", {"start": v(3.16, 5.62) * mm, "end": v(6.45, 0.07) * mm});
            skLineSegment(sketch, "E47.1", {"start": v(6.45, 0.07) * mm, "end": v(3.29, -5.55) * mm});
            skLineSegment(sketch, "E47.2", {"start": v(3.29, -5.55) * mm, "end": v(-3.16, -5.62) * mm});
            skLineSegment(sketch, "E47.3", {"start": v(-3.16, -5.62) * mm, "end": v(-6.45, -0.07) * mm});
            skLineSegment(sketch, "E47.4", {"start": v(-6.45, -0.07) * mm, "end": v(-3.29, 5.55) * mm});
            skLineSegment(sketch, "E47.5", {"start": v(-3.29, 5.55) * mm, "end": v(3.16, 5.62) * mm});
            skSolve(sketch);
        }
        {
            var Q0;
            Q0 = qSketchRegion(id + "F4", true);
            extrude(context, id + "F5", {"entities" : qUnion([Q0]), "operationType" : NewBodyOperationType.REMOVE, "oppositeDirection" : true, "depth" : 254 * mm});
        }
    });
